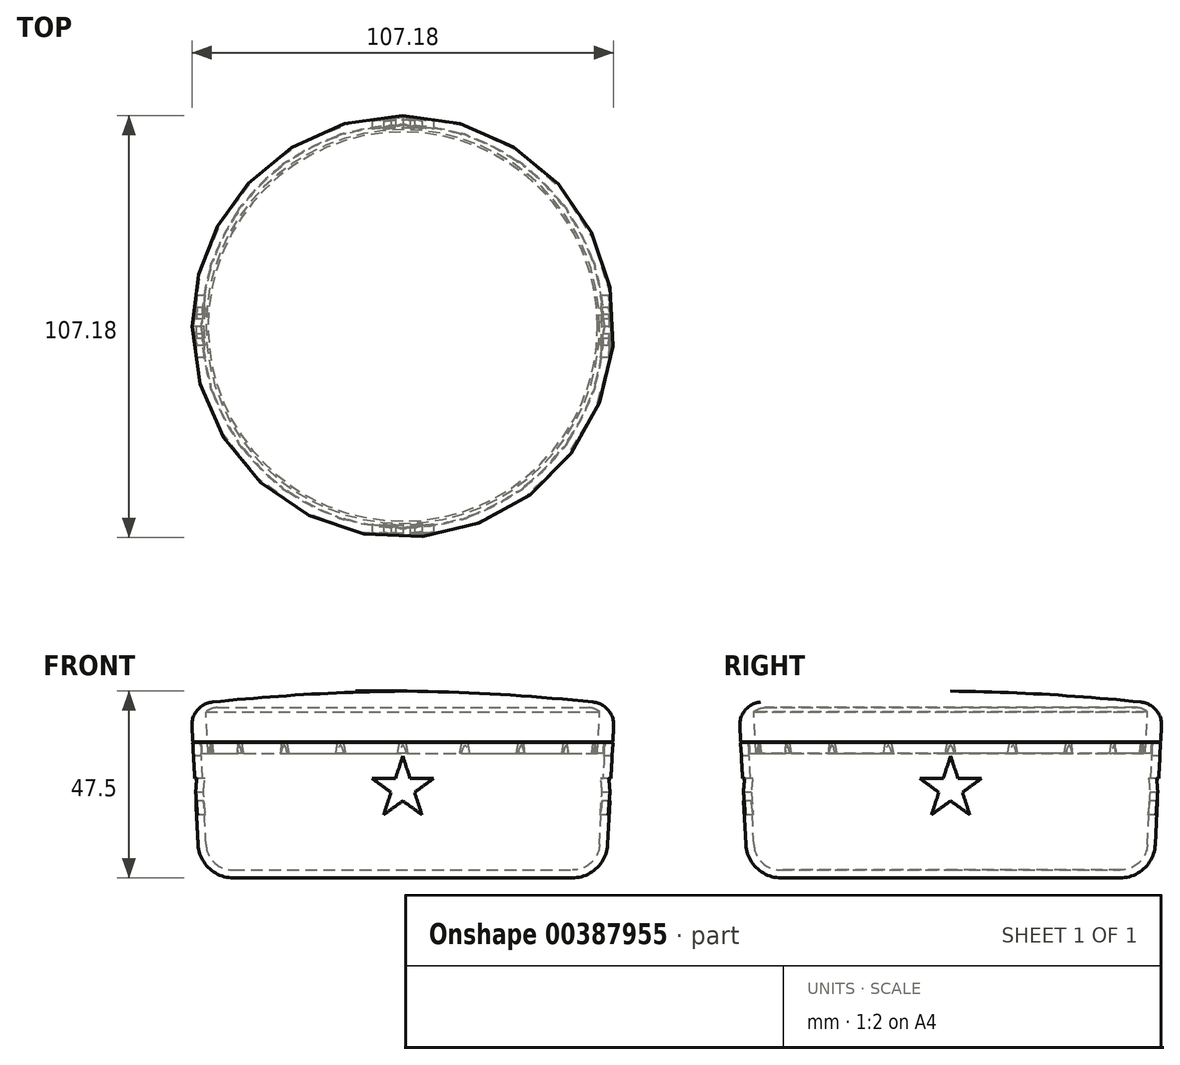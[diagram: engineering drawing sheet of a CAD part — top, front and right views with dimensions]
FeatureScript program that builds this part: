
annotation { "Feature Type Name" : "Feature", "Feature Type Description" : "" }
export const myFeature = defineFeature(function(context is Context, id is Id, definition is map)
    precondition{}
    {
        {
            var Q0;
            Q0=qCreatedBy(makeId("Front.planeOp"),FACE);
            var sketch = newSketch(context, id + "F0", { "sketchPlane" : qUnion([Q0])});
            skLineSegment(sketch, "E0", {"start": v(0, -8.48) * mm, "end": v(43.06, -8.48) * mm});
            skLineSegment(sketch, "E1", {"start": v(53.58, 30.1) * mm, "end": v(52, 0) * mm});
            skArc(sketch, "E2", {"start": v(43.06, -8.48) * mm, "mid": v(49.22, -6.02) * mm, "end": v(52, 0) * mm});
            skArc(sketch, "E3", {"start": v(53.58, 30.1) * mm, "mid": v(52.2, 34.19) * mm, "end": v(48.38, 36.2) * mm});
            skLineSegment(sketch, "E4", {"start": v(0, -6.48) * mm, "end": v(43.17, -6.48) * mm});
            skLineSegment(sketch, "E5", {"start": v(0, 34.78) * mm, "end": v(47.14, 34.78) * mm});
            skLineSegment(sketch, "E6", {"start": v(50, 0) * mm, "end": v(51.58, 30.1) * mm});
            skArc(sketch, "E7", {"start": v(51.58, 30.1) * mm, "mid": v(50.36, 33.4) * mm, "end": v(47.14, 34.78) * mm});
            skArc(sketch, "E8", {"start": v(43.17, -6.48) * mm, "mid": v(47.88, -4.6) * mm, "end": v(50, 0) * mm});
            skLineSegment(sketch, "E9", {"start": v(0, 34.78) * mm, "end": v(0, 39.02) * mm});
            skLineSegment(sketch, "E10", {"start": v(0, -6.48) * mm, "end": v(0, -8.48) * mm});
            skArc(sketch, "E11", {"start": v(48.38, 36.2) * mm, "mid": v(24.22, 38.15) * mm, "end": v(0, 38.99) * mm});
            skLineSegment(sketch, "E12", {"start": v(0, 39.02) * mm, "end": v(-5.88, 39.02) * mm, "construction": true});
            skLineSegment(sketch, "E13", {"start": v(51.37, 26.1) * mm, "end": v(53.37, 26.1) * mm});
            skLineSegment(sketch, "E14", {"start": v(51.36, 26) * mm, "end": v(53.36, 26) * mm});
            skLineSegment(sketch, "E15", {"start": v(51.37, 26.1) * mm, "end": v(51.12, 26.1) * mm});
            skLineSegment(sketch, "E16", {"start": v(51.12, 26.1) * mm, "end": v(50.96, 23.11) * mm});
            skLineSegment(sketch, "E17", {"start": v(50.96, 23.11) * mm, "end": v(49.46, 23.11) * mm});
            skLineSegment(sketch, "E18", {"start": v(49.46, 23.11) * mm, "end": v(50.01, 33.73) * mm});
            skSolve(sketch);
        }
        {
            var Q0;
            {var subQ5=sQuery(id+"F0.wireOp",EDGE,"E3");Q0=makeQuery(id+"F0.imprint","IMPRINT",FACE,{"disambiguationData":[TD([[makeQuery(id+"F0.imprint","IMPRINT",EDGE,{"derivedFrom":subQ5}),1.0]])]});}
            var Q1;
            {var subQ0=sQuery(id+"F0.wireOp",EDGE,"E15");Q1=makeQuery(id+"F0.imprint","IMPRINT",FACE,{"disambiguationData":[TD([[makeQuery(id+"F0.imprint","IMPRINT",EDGE,{"derivedFrom":subQ0}),-1.0]])]});}
            var Q2;
            Q2=makeQuery(id+"F0.imprint","IMPRINT",FACE,{"disambiguationData":[TD([[makeQuery(id+"F0.imprint","IMPRINT",EDGE,{"derivedFrom":sQuery(id+"F0.wireOp",EDGE,"E0")}),1.0]])]});
            var Q3;
            Q3=sQuery(id+"F0.wireOp",EDGE,"E9");
            revolve(context, id + "F1", {"entities" : qUnion([Q0, Q1, Q2]), "axis" : qUnion([Q3]), "revolveType" : RevolveType.FULL});
        }
        {
            var Q0;
            Q0=makeQuery(id+"F1.opRevolve","SWEPT_FACE",FACE,{"disambiguationData":[OSD([sQuery(id+"F0.wireOp",EDGE,"E13"),sQuery(id+"F0.wireOp",EDGE,"E15")])]});
            var sketch = newSketch(context, id + "F2", { "sketchPlane" : qUnion([Q0])});
            skArc(sketch, "E19", {"start": v(0.75, 51.1) * mm, "mid": v(0, 51.27) * mm, "end": v(-0.75, 51.1) * mm});
            skLineSegment(sketch, "E20", {"start": v(0, 55.66) * mm, "end": v(0, 46.37) * mm, "construction": true});
            skArc(sketch, "E21.1.0", {"start": v(16.5, 48.38) * mm, "mid": v(15.84, 48.76) * mm, "end": v(15.08, 48.84) * mm});
            skArc(sketch, "E21.2.0", {"start": v(30.65, 40.9) * mm, "mid": v(30.13, 41.47) * mm, "end": v(29.43, 41.79) * mm});
            skArc(sketch, "E21.3.0", {"start": v(41.79, 29.43) * mm, "mid": v(41.47, 30.13) * mm, "end": v(40.9, 30.65) * mm});
            skArc(sketch, "E21.4.0", {"start": v(48.84, 15.08) * mm, "mid": v(48.76, 15.84) * mm, "end": v(48.38, 16.5) * mm});
            skArc(sketch, "E21.5.0", {"start": v(51.1, -0.75) * mm, "mid": v(51.27, 0) * mm, "end": v(51.1, 0.75) * mm});
            skArc(sketch, "E21.6.0", {"start": v(48.38, -16.5) * mm, "mid": v(48.76, -15.84) * mm, "end": v(48.84, -15.08) * mm});
            skArc(sketch, "E21.7.0", {"start": v(40.9, -30.65) * mm, "mid": v(41.47, -30.13) * mm, "end": v(41.79, -29.43) * mm});
            skArc(sketch, "E21.8.0", {"start": v(29.43, -41.79) * mm, "mid": v(30.13, -41.47) * mm, "end": v(30.65, -40.9) * mm});
            skArc(sketch, "E21.9.0", {"start": v(15.08, -48.84) * mm, "mid": v(15.84, -48.76) * mm, "end": v(16.5, -48.38) * mm});
            skArc(sketch, "E21.10.0", {"start": v(-0.75, -51.1) * mm, "mid": v(0, -51.27) * mm, "end": v(0.75, -51.1) * mm});
            skArc(sketch, "E21.11.0", {"start": v(-16.5, -48.38) * mm, "mid": v(-15.84, -48.76) * mm, "end": v(-15.08, -48.84) * mm});
            skArc(sketch, "E21.12.0", {"start": v(-30.65, -40.9) * mm, "mid": v(-30.13, -41.47) * mm, "end": v(-29.43, -41.79) * mm});
            skArc(sketch, "E21.13.0", {"start": v(-41.79, -29.43) * mm, "mid": v(-41.47, -30.13) * mm, "end": v(-40.9, -30.65) * mm});
            skArc(sketch, "E21.14.0", {"start": v(-48.84, -15.08) * mm, "mid": v(-48.76, -15.84) * mm, "end": v(-48.38, -16.5) * mm});
            skArc(sketch, "E21.15.0", {"start": v(-51.1, 0.75) * mm, "mid": v(-51.27, 0) * mm, "end": v(-51.1, -0.75) * mm});
            skArc(sketch, "E21.16.0", {"start": v(-48.38, 16.5) * mm, "mid": v(-48.76, 15.84) * mm, "end": v(-48.84, 15.08) * mm});
            skArc(sketch, "E21.17.0", {"start": v(-40.9, 30.65) * mm, "mid": v(-41.47, 30.13) * mm, "end": v(-41.79, 29.43) * mm});
            skArc(sketch, "E21.18.0", {"start": v(-29.43, 41.79) * mm, "mid": v(-30.13, 41.47) * mm, "end": v(-30.65, 40.9) * mm});
            skPoint(sketch, "E21.center", {"position": v(0, 0) * mm});
            skLineSegment(sketch, "E21.anchor1", {"start": v(0, 0) * mm, "end": v(0, 49.38) * mm, "construction": true});
            skLineSegment(sketch, "E21.anchor2", {"start": v(0, 0) * mm, "end": v(-15.26, 46.96) * mm, "construction": true});
            skArc(sketch, "E22.1.19.0", {"start": v(-15.08, 48.84) * mm, "mid": v(-15.84, 48.76) * mm, "end": v(-16.5, 48.38) * mm});
            skSolve(sketch);
        }
        {
            var Q0;
            {var subQ0=sQuery(id+"F2.wireOp",EDGE,"E19");Q0=makeQuery(id+"F2.imprint","IMPRINT",FACE,{"disambiguationData":[TD([[makeQuery(id+"F2.imprint","IMPRINT",EDGE,{"derivedFrom":subQ0}),1.0]])]});}
            var Q1;
            {var subQ0=sQuery(id+"F2.wireOp",EDGE,"E21.1.0");Q1=makeQuery(id+"F2.imprint","IMPRINT",FACE,{"disambiguationData":[TD([[makeQuery(id+"F2.imprint","IMPRINT",EDGE,{"derivedFrom":subQ0}),1.0]])]});}
            var Q2;
            {var subQ0=sQuery(id+"F2.wireOp",EDGE,"E21.2.0");Q2=makeQuery(id+"F2.imprint","IMPRINT",FACE,{"disambiguationData":[TD([[makeQuery(id+"F2.imprint","IMPRINT",EDGE,{"derivedFrom":subQ0}),1.0]])]});}
            var Q3;
            {var subQ0=sQuery(id+"F2.wireOp",EDGE,"E21.3.0");Q3=makeQuery(id+"F2.imprint","IMPRINT",FACE,{"disambiguationData":[TD([[makeQuery(id+"F2.imprint","IMPRINT",EDGE,{"derivedFrom":subQ0}),1.0]])]});}
            var Q4;
            {var subQ0=sQuery(id+"F2.wireOp",EDGE,"E21.4.0");Q4=makeQuery(id+"F2.imprint","IMPRINT",FACE,{"disambiguationData":[TD([[makeQuery(id+"F2.imprint","IMPRINT",EDGE,{"derivedFrom":subQ0}),1.0]])]});}
            var Q5;
            {var subQ0=sQuery(id+"F2.wireOp",EDGE,"E21.5.0");Q5=makeQuery(id+"F2.imprint","IMPRINT",FACE,{"disambiguationData":[TD([[makeQuery(id+"F2.imprint","IMPRINT",EDGE,{"derivedFrom":subQ0}),1.0]])]});}
            var Q6;
            {var subQ0=sQuery(id+"F2.wireOp",EDGE,"E21.6.0");Q6=makeQuery(id+"F2.imprint","IMPRINT",FACE,{"disambiguationData":[TD([[makeQuery(id+"F2.imprint","IMPRINT",EDGE,{"derivedFrom":subQ0}),1.0]])]});}
            var Q7;
            {var subQ0=sQuery(id+"F2.wireOp",EDGE,"E21.7.0");Q7=makeQuery(id+"F2.imprint","IMPRINT",FACE,{"disambiguationData":[TD([[makeQuery(id+"F2.imprint","IMPRINT",EDGE,{"derivedFrom":subQ0}),1.0]])]});}
            var Q8;
            {var subQ0=sQuery(id+"F2.wireOp",EDGE,"E21.8.0");Q8=makeQuery(id+"F2.imprint","IMPRINT",FACE,{"disambiguationData":[TD([[makeQuery(id+"F2.imprint","IMPRINT",EDGE,{"derivedFrom":subQ0}),1.0]])]});}
            var Q9;
            {var subQ0=sQuery(id+"F2.wireOp",EDGE,"E21.9.0");Q9=makeQuery(id+"F2.imprint","IMPRINT",FACE,{"disambiguationData":[TD([[makeQuery(id+"F2.imprint","IMPRINT",EDGE,{"derivedFrom":subQ0}),1.0]])]});}
            var Q10;
            {var subQ0=sQuery(id+"F2.wireOp",EDGE,"E21.10.0");Q10=makeQuery(id+"F2.imprint","IMPRINT",FACE,{"disambiguationData":[TD([[makeQuery(id+"F2.imprint","IMPRINT",EDGE,{"derivedFrom":subQ0}),1.0]])]});}
            var Q11;
            {var subQ0=sQuery(id+"F2.wireOp",EDGE,"E21.11.0");Q11=makeQuery(id+"F2.imprint","IMPRINT",FACE,{"disambiguationData":[TD([[makeQuery(id+"F2.imprint","IMPRINT",EDGE,{"derivedFrom":subQ0}),1.0]])]});}
            var Q12;
            {var subQ0=sQuery(id+"F2.wireOp",EDGE,"E21.12.0");Q12=makeQuery(id+"F2.imprint","IMPRINT",FACE,{"disambiguationData":[TD([[makeQuery(id+"F2.imprint","IMPRINT",EDGE,{"derivedFrom":subQ0}),1.0]])]});}
            var Q13;
            {var subQ0=sQuery(id+"F2.wireOp",EDGE,"E21.13.0");Q13=makeQuery(id+"F2.imprint","IMPRINT",FACE,{"disambiguationData":[TD([[makeQuery(id+"F2.imprint","IMPRINT",EDGE,{"derivedFrom":subQ0}),1.0]])]});}
            var Q14;
            {var subQ0=sQuery(id+"F2.wireOp",EDGE,"E21.14.0");Q14=makeQuery(id+"F2.imprint","IMPRINT",FACE,{"disambiguationData":[TD([[makeQuery(id+"F2.imprint","IMPRINT",EDGE,{"derivedFrom":subQ0}),1.0]])]});}
            var Q15;
            {var subQ0=sQuery(id+"F2.wireOp",EDGE,"E21.15.0");Q15=makeQuery(id+"F2.imprint","IMPRINT",FACE,{"disambiguationData":[TD([[makeQuery(id+"F2.imprint","IMPRINT",EDGE,{"derivedFrom":subQ0}),1.0]])]});}
            var Q16;
            {var subQ0=sQuery(id+"F2.wireOp",EDGE,"E21.16.0");Q16=makeQuery(id+"F2.imprint","IMPRINT",FACE,{"disambiguationData":[TD([[makeQuery(id+"F2.imprint","IMPRINT",EDGE,{"derivedFrom":subQ0}),1.0]])]});}
            var Q17;
            {var subQ0=sQuery(id+"F2.wireOp",EDGE,"E21.17.0");Q17=makeQuery(id+"F2.imprint","IMPRINT",FACE,{"disambiguationData":[TD([[makeQuery(id+"F2.imprint","IMPRINT",EDGE,{"derivedFrom":subQ0}),1.0]])]});}
            var Q18;
            {var subQ0=sQuery(id+"F2.wireOp",EDGE,"E21.18.0");Q18=makeQuery(id+"F2.imprint","IMPRINT",FACE,{"disambiguationData":[TD([[makeQuery(id+"F2.imprint","IMPRINT",EDGE,{"derivedFrom":subQ0}),1.0]])]});}
            var Q19;
            {var subQ0=sQuery(id+"F2.wireOp",EDGE,"E22.1.19.0");Q19=makeQuery(id+"F2.imprint","IMPRINT",FACE,{"disambiguationData":[TD([[makeQuery(id+"F2.imprint","IMPRINT",EDGE,{"derivedFrom":subQ0}),1.0]])]});}
            var Q20;
            Q20=makeQuery(id+"F1.opRevolve","SWEPT_FACE",FACE,{"disambiguationData":[OSD([sQuery(id+"F0.wireOp",EDGE,"E17")])]});
            extrude(context, id + "F3", {"entities" : qUnion([Q0, Q1, Q2, Q3, Q4, Q5, Q6, Q7, Q8, Q9, Q10, Q11, Q12, Q13, Q14, Q15, Q16, Q17, Q18, Q19]), "operationType" : NewBodyOperationType.ADD, "endBound" : BoundingType.UP_TO_SURFACE, "endBoundEntityFace" : qUnion([Q20]), "depth" : 25 * mm, "hasDraft" : true, "draftAngle" : 3 * degree});
        }
        {
            var Q0;
            Q0=qCreatedBy(makeId("Front.planeOp"),FACE);
            var sketch = newSketch(context, id + "F4", { "sketchPlane" : qUnion([Q0])});
            skLineSegment(sketch, "E23", {"start": v(0, 22.5) * mm, "end": v(-1.85, 16.8) * mm});
            skLineSegment(sketch, "E24", {"start": v(-1.85, 16.8) * mm, "end": v(-7.85, 16.8) * mm});
            skLineSegment(sketch, "E25", {"start": v(-7.85, 16.8) * mm, "end": v(-3, 13.27) * mm});
            skLineSegment(sketch, "E26", {"start": v(-3, 13.27) * mm, "end": v(-4.85, 7.57) * mm});
            skLineSegment(sketch, "E27", {"start": v(-4.85, 7.57) * mm, "end": v(0, 11.1) * mm});
            skLineSegment(sketch, "E28", {"start": v(0, 11.1) * mm, "end": v(4.85, 7.57) * mm});
            skLineSegment(sketch, "E29", {"start": v(4.85, 7.57) * mm, "end": v(3, 13.27) * mm});
            skLineSegment(sketch, "E30", {"start": v(3, 13.27) * mm, "end": v(7.85, 16.8) * mm});
            skLineSegment(sketch, "E31", {"start": v(7.85, 16.8) * mm, "end": v(1.85, 16.8) * mm});
            skLineSegment(sketch, "E32", {"start": v(1.85, 16.8) * mm, "end": v(0, 22.5) * mm});
            skPoint(sketch, "E33", {"position": v(0, 22.5) * mm});
            skSolve(sketch);
        }
        {
            var Q0;
            Q0=makeQuery(id+"F4.imprint","IMPRINT",FACE,{"disambiguationData":[TD([[makeQuery(id+"F4.imprint","IMPRINT",EDGE,{"derivedFrom":sQuery(id+"F4.wireOp",EDGE,"E23")}),1.0]])]});
            extrude(context, id + "F5", {"entities" : qUnion([Q0]), "operationType" : NewBodyOperationType.REMOVE, "endBound" : BoundingType.SYMMETRIC, "oppositeDirection" : true, "depth" : 120 * mm});
        }
        {
            var Q0;
            Q0=qCreatedBy(makeId("Right.planeOp"),FACE);
            var sketch = newSketch(context, id + "F6", { "sketchPlane" : qUnion([Q0])});
            skLineSegment(sketch, "E34", {"start": v(0, 22.5) * mm, "end": v(-1.85, 16.8) * mm});
            skLineSegment(sketch, "E35", {"start": v(-1.85, 16.8) * mm, "end": v(-7.85, 16.8) * mm});
            skLineSegment(sketch, "E36", {"start": v(-7.85, 16.8) * mm, "end": v(-3, 13.27) * mm});
            skLineSegment(sketch, "E37", {"start": v(-3, 13.27) * mm, "end": v(-4.85, 7.57) * mm});
            skLineSegment(sketch, "E38", {"start": v(-4.85, 7.57) * mm, "end": v(0, 11.1) * mm});
            skLineSegment(sketch, "E39", {"start": v(0, 11.1) * mm, "end": v(4.85, 7.57) * mm});
            skLineSegment(sketch, "E40", {"start": v(4.85, 7.57) * mm, "end": v(3, 13.27) * mm});
            skLineSegment(sketch, "E41", {"start": v(3, 13.27) * mm, "end": v(7.85, 16.8) * mm});
            skLineSegment(sketch, "E42", {"start": v(7.85, 16.8) * mm, "end": v(1.85, 16.8) * mm});
            skLineSegment(sketch, "E43", {"start": v(1.85, 16.8) * mm, "end": v(0, 22.5) * mm});
            skSolve(sketch);
        }
        {
            var Q0;
            Q0 = qSketchRegion(id + "F6", true);
            extrude(context, id + "F7", {"entities" : qUnion([Q0]), "operationType" : NewBodyOperationType.REMOVE, "endBound" : BoundingType.SYMMETRIC, "depth" : 120 * mm});
        }
        {
            var Q0;
            Q0=makeQuery(id+"F1.opRevolve","SWEPT_EDGE",EDGE,{"disambiguationData":[OSD([sQuery(id+"F0.wireOp",EDGE,"E1"),sQuery(id+"F0.wireOp",EDGE,"E14")])]});
            var Q1;
            Q1=makeQuery(id+"F1.opRevolve","SWEPT_EDGE",EDGE,{"disambiguationData":[OSD([sQuery(id+"F0.wireOp",EDGE,"E6"),sQuery(id+"F0.wireOp",EDGE,"E14")])]});
            fillet(context, id + "F8", {"entities" : qUnion([Q0, Q1]), "radius" : 0.3 * mm, "tangentPropagation" : true, "allowEdgeOverflow" : false});
        }
        {
            var Q0;
            Q0=makeQuery(id+"F1.opRevolve","SWEPT_EDGE",EDGE,{"disambiguationData":[OSD([sQuery(id+"F0.wireOp",EDGE,"E1"),sQuery(id+"F0.wireOp",EDGE,"E13")])]});
            fillet(context, id + "F9", {"entities" : qUnion([Q0]), "radius" : 0.3 * mm, "tangentPropagation" : true, "allowEdgeOverflow" : false});
        }
    });
